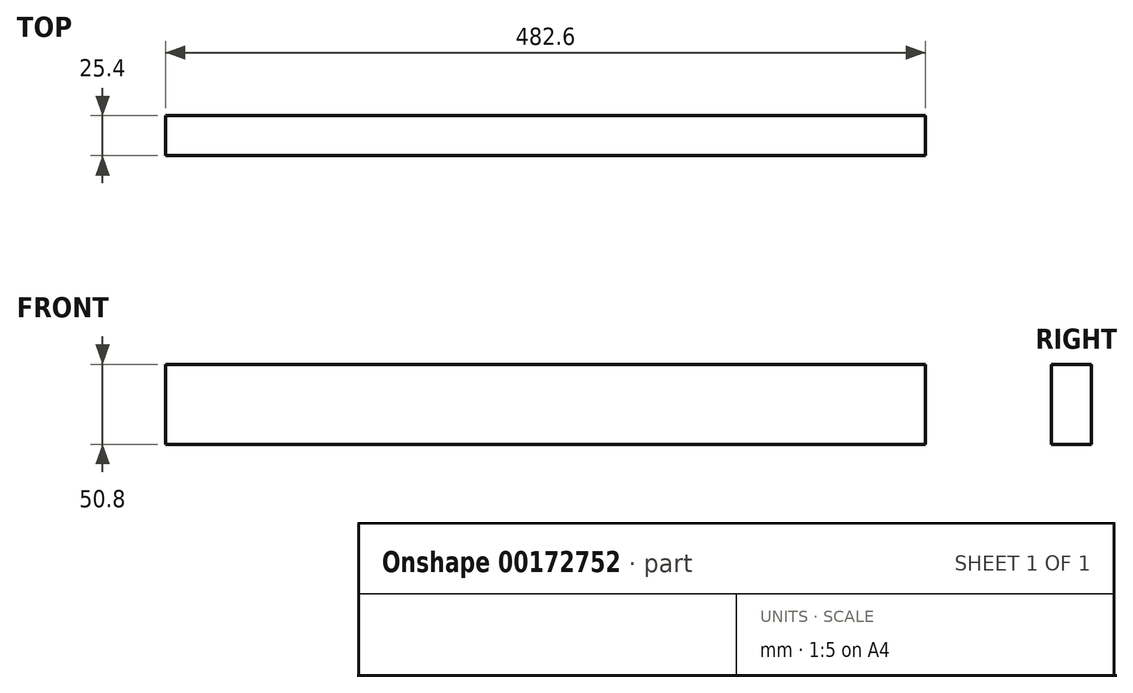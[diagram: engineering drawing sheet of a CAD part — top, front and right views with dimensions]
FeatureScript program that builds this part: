
annotation { "Feature Type Name" : "Feature", "Feature Type Description" : "" }
export const myFeature = defineFeature(function(context is Context, id is Id, definition is map)
    precondition{}
    {
        {
            var Q0;
            Q0=qCreatedBy(makeId("Front.planeOp"),FACE);
            var sketch = newSketch(context, id + "F0", { "sketchPlane" : qUnion([Q0])});
            skLineSegment(sketch, "E0.bottom", {"start": v(-237.98, 73.14) * mm, "end": v(244.62, 73.14) * mm});
            skLineSegment(sketch, "E0.top", {"start": v(-237.98, 22.34) * mm, "end": v(244.62, 22.34) * mm});
            skLineSegment(sketch, "E0.left", {"start": v(-237.98, 73.14) * mm, "end": v(-237.98, 22.34) * mm});
            skLineSegment(sketch, "E0.right", {"start": v(244.62, 73.14) * mm, "end": v(244.62, 22.34) * mm});
            skSolve(sketch);
        }
        {
            var Q0;
            Q0 = qSketchRegion(id + "F0", true);
            extrude(context, id + "F1", {"entities" : qUnion([Q0]), "depth" : 25.4 * mm});
        }
    });
